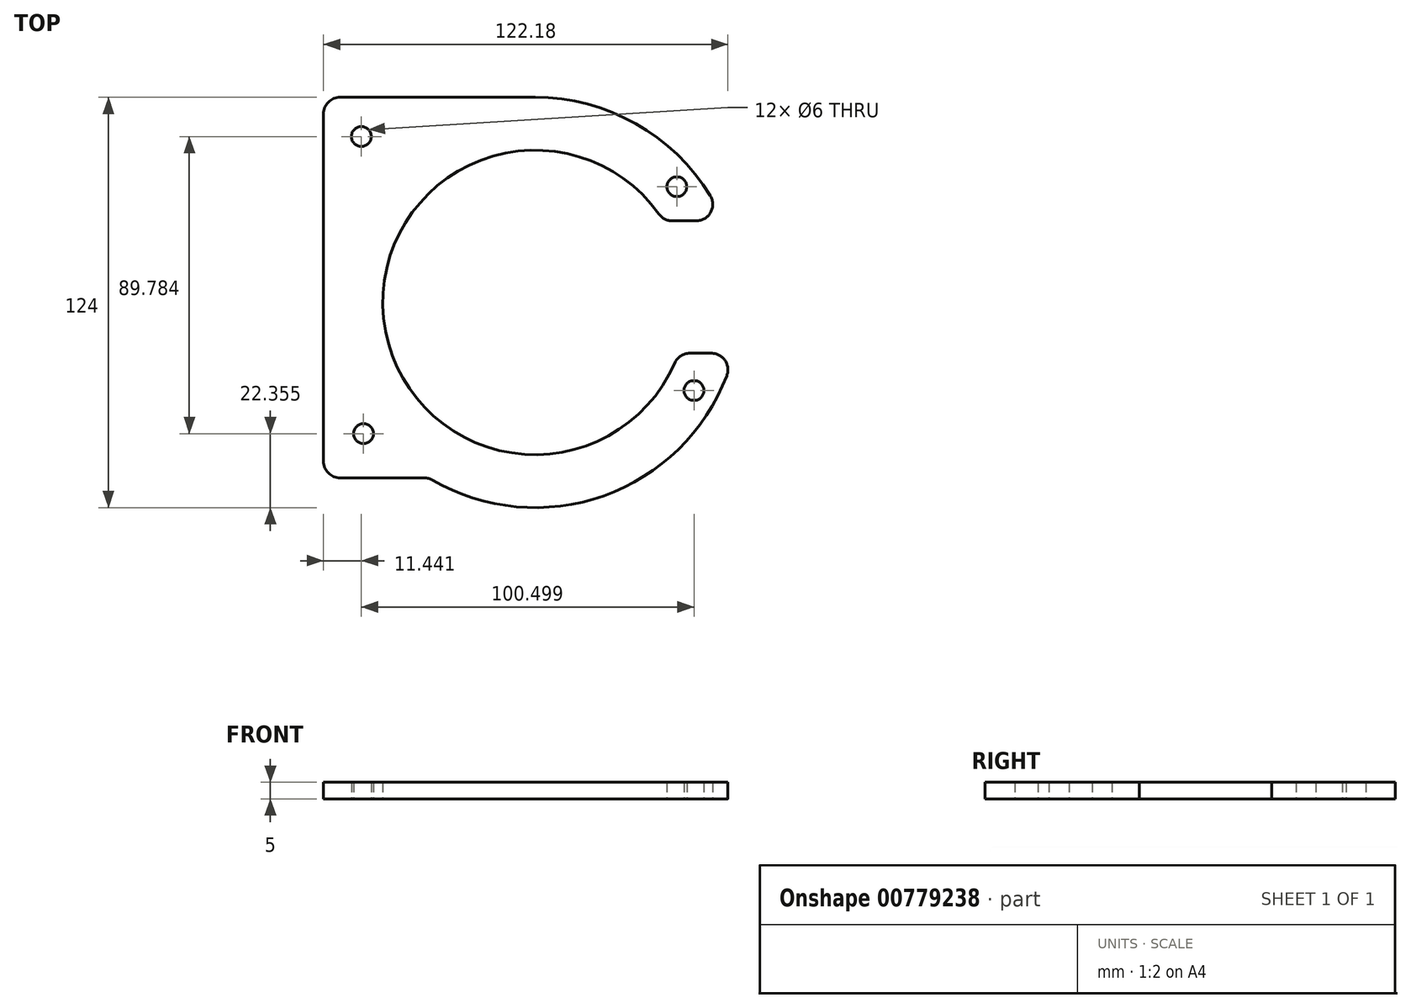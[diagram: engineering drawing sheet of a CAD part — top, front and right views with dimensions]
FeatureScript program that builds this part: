
annotation { "Feature Type Name" : "Feature", "Feature Type Description" : "" }
export const myFeature = defineFeature(function(context is Context, id is Id, definition is map)
    precondition{}
    {
        {
            var Q0;
            Q0=qCreatedBy(makeId("Top.planeOp"),FACE);
            var sketch = newSketch(context, id + "F0", { "sketchPlane" : qUnion([Q0])});
            skArc(sketch, "E0", {"start": v(37.42, 26.75) * mm, "mid": v(-45.75, -4.83) * mm, "end": v(42.18, -18.35) * mm});
            skArc(sketch, "E1", {"start": v(-31.04, -53.67) * mm, "mid": v(20.72, -58.43) * mm, "end": v(57.92, -22.13) * mm});
            skLineSegment(sketch, "E2", {"start": v(0, 62) * mm, "end": v(-58.93, 62) * mm});
            skLineSegment(sketch, "E3", {"start": v(-63.93, 57) * mm, "end": v(-63.93, -48) * mm});
            skLineSegment(sketch, "E4", {"start": v(-58.93, -53) * mm, "end": v(-33.54, -53) * mm});
            skLineSegment(sketch, "E5", {"start": v(48.68, 24.66) * mm, "end": v(41.49, 24.66) * mm});
            skLineSegment(sketch, "E6", {"start": v(46.77, -15.34) * mm, "end": v(53.25, -15.34) * mm});
            skArc(sketch, "E7.trimOffspring", {"start": v(52.95, 32.26) * mm, "mid": v(30.36, 54.06) * mm, "end": v(0, 62) * mm});
            skPoint(sketch, "E8.visualSharp", {"position": v(-63.93, 62) * mm});
            skArc(sketch, "E8.filletArc", {"start": v(-58.93, 62) * mm, "mid": v(-62.46, 60.54) * mm, "end": v(-63.93, 57) * mm});
            skPoint(sketch, "E9.visualSharp", {"position": v(-63.93, -53) * mm});
            skArc(sketch, "E9.filletArc", {"start": v(-63.93, -48) * mm, "mid": v(-62.46, -51.54) * mm, "end": v(-58.93, -53) * mm});
            skPoint(sketch, "E10.visualSharp", {"position": v(-32.17, -53) * mm});
            skArc(sketch, "E10.filletArc", {"start": v(-31.04, -53.67) * mm, "mid": v(-32.25, -53.17) * mm, "end": v(-33.54, -53) * mm});
            skPoint(sketch, "E11.visualSharp", {"position": v(38.83, 24.66) * mm});
            skArc(sketch, "E11.filletArc", {"start": v(37.42, 26.75) * mm, "mid": v(39.2, 25.21) * mm, "end": v(41.49, 24.66) * mm});
            skPoint(sketch, "E12.visualSharp", {"position": v(56.89, 24.66) * mm});
            skArc(sketch, "E12.filletArc", {"start": v(48.68, 24.66) * mm, "mid": v(53.04, 27.21) * mm, "end": v(52.95, 32.26) * mm});
            skPoint(sketch, "E13.visualSharp", {"position": v(60.07, -15.34) * mm});
            skArc(sketch, "E13.filletArc", {"start": v(57.92, -22.13) * mm, "mid": v(57.37, -17.5) * mm, "end": v(53.25, -15.34) * mm});
            skPoint(sketch, "E14.visualSharp", {"position": v(43.37, -15.34) * mm});
            skArc(sketch, "E14.filletArc", {"start": v(46.77, -15.34) * mm, "mid": v(44.03, -16.16) * mm, "end": v(42.18, -18.35) * mm});
            skCircle(sketch, "E15", {"center": v(-52.49, 50.14) * mm, "radius": 3 * mm});
            skCircle(sketch, "E16", {"center": v(-51.83, -39.64) * mm, "radius": 3 * mm});
            skCircle(sketch, "E17", {"center": v(42.84, 34.98) * mm, "radius": 3 * mm});
            skCircle(sketch, "E18", {"center": v(48.01, -26.62) * mm, "radius": 3 * mm});
            skSolve(sketch);
        }
        {
            var Q0;
            Q0=makeQuery(id+"F0.imprint","IMPRINT",FACE,{"disambiguationData":[TD([[makeQuery(id+"F0.imprint","IMPRINT",EDGE,{"derivedFrom":sQuery(id+"F0.wireOp",EDGE,"E0")}),-1.0]])]});
            extrude(context, id + "F1", {"entities" : qUnion([Q0]), "depth" : 5 * mm, "offsetDistance" : 25 * mm});
        }
    });
